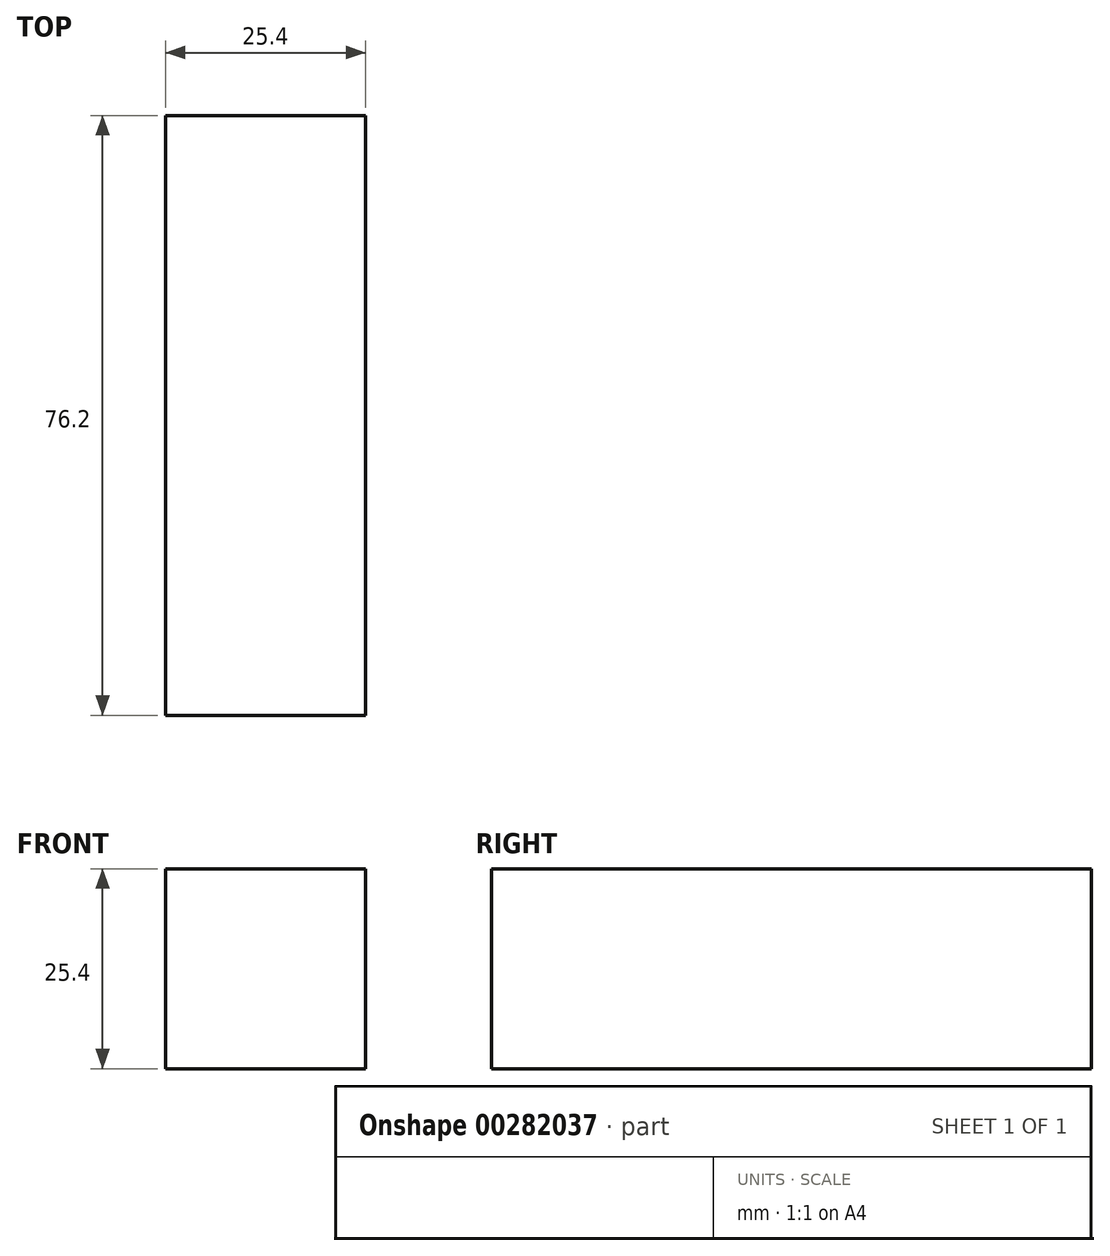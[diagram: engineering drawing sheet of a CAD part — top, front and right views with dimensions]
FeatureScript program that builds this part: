
annotation { "Feature Type Name" : "Feature", "Feature Type Description" : "" }
export const myFeature = defineFeature(function(context is Context, id is Id, definition is map)
    precondition{}
    {
        {
            var Q0;
            Q0=qCreatedBy(makeId("Front.planeOp"),FACE);
            var sketch = newSketch(context, id + "F0", { "sketchPlane" : qUnion([Q0])});
            skLineSegment(sketch, "E0.bottom", {"start": v(-47.93, 47.55) * mm, "end": v(-22.53, 47.55) * mm});
            skLineSegment(sketch, "E0.top", {"start": v(-47.93, 22.15) * mm, "end": v(-22.53, 22.15) * mm});
            skLineSegment(sketch, "E0.left", {"start": v(-47.93, 47.55) * mm, "end": v(-47.93, 22.15) * mm});
            skLineSegment(sketch, "E0.right", {"start": v(-22.53, 47.55) * mm, "end": v(-22.53, 22.15) * mm});
            skSolve(sketch);
        }
        {
            var Q0;
            Q0=makeQuery(id+"F0.imprint","IMPRINT",FACE,{"disambiguationData":[TD([[makeQuery(id+"F0.imprint","IMPRINT",EDGE,{"derivedFrom":sQuery(id+"F0.wireOp",EDGE,"E0.bottom")}),-1.0]])]});
            extrude(context, id + "F1", {"entities" : qUnion([Q0]), "depth" : 76.2 * mm});
        }
    });
